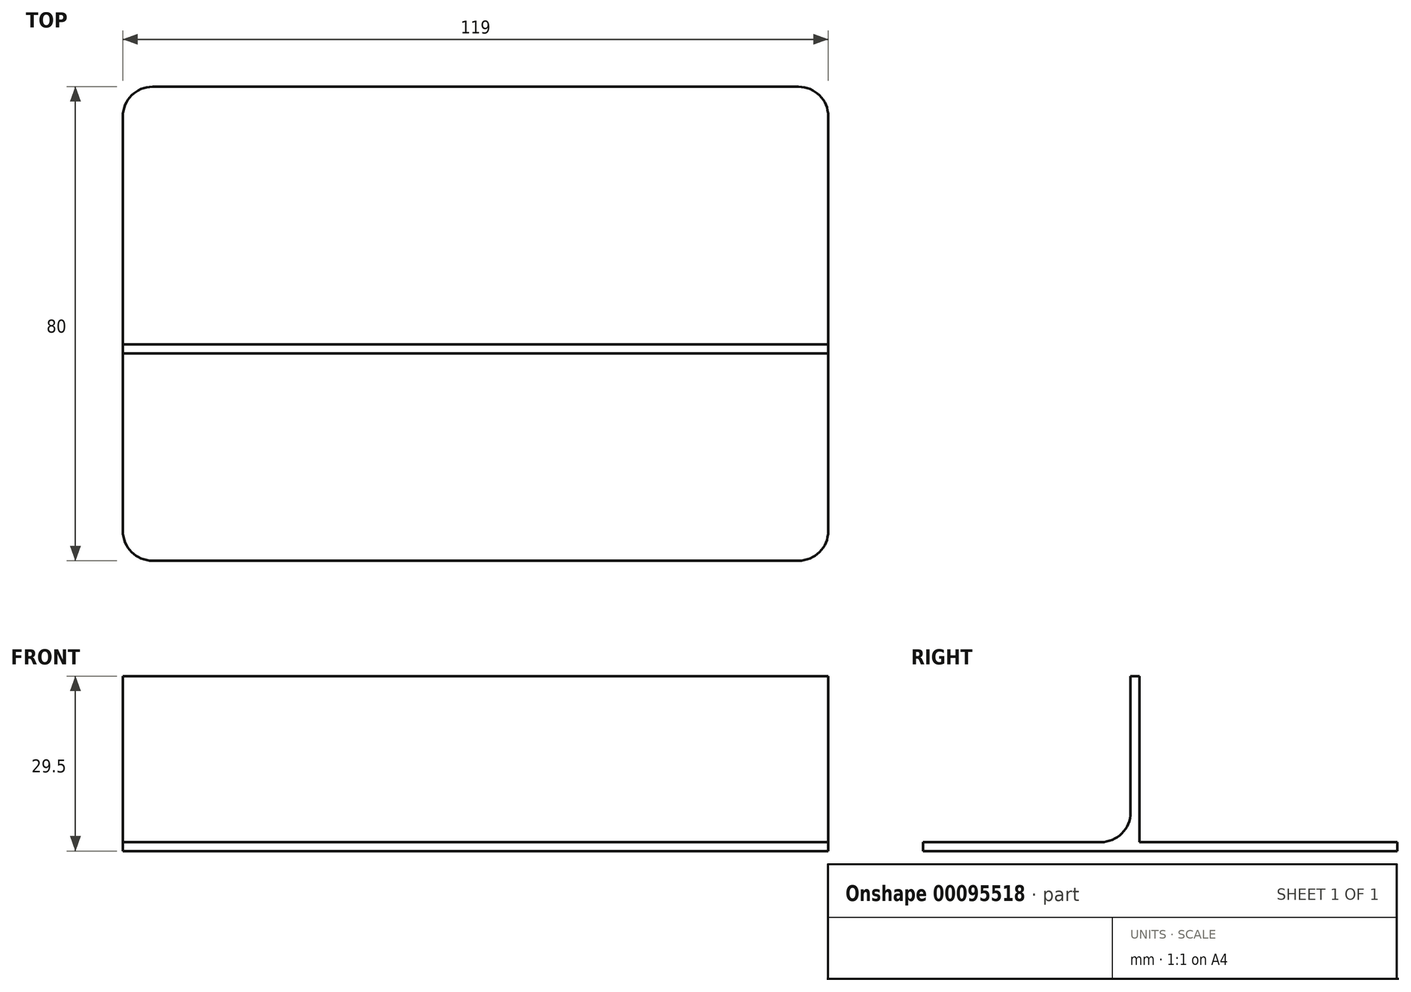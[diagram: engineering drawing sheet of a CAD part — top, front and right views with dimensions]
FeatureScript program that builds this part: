
annotation { "Feature Type Name" : "Feature", "Feature Type Description" : "" }
export const myFeature = defineFeature(function(context is Context, id is Id, definition is map)
    precondition{}
    {
        {
            var Q0;
            Q0=qCreatedBy(makeId("Top.planeOp"),FACE);
            var sketch = newSketch(context, id + "F0", { "sketchPlane" : qUnion([Q0])});
            skLineSegment(sketch, "E0.bottom", {"start": v(-85.63, 36.48) * mm, "end": v(33.37, 36.48) * mm});
            skLineSegment(sketch, "E0.top", {"start": v(-85.63, -43.52) * mm, "end": v(33.37, -43.52) * mm});
            skLineSegment(sketch, "E0.left", {"start": v(-85.63, 36.48) * mm, "end": v(-85.63, -43.52) * mm});
            skLineSegment(sketch, "E0.right", {"start": v(33.37, 36.48) * mm, "end": v(33.37, -43.52) * mm});
            skSolve(sketch);
        }
        {
            var Q0;
            Q0 = qSketchRegion(id + "F0", true);
            extrude(context, id + "F1", {"entities" : qUnion([Q0]), "depth" : 1.5 * mm});
        }
        {
            var Q0;
            Q0=makeQuery(id+"F1.opExtrude","SWEPT_EDGE",EDGE,{"disambiguationData":[OSD([sQuery(id+"F0.wireOp",EDGE,"E0.top"),sQuery(id+"F0.wireOp",EDGE,"E0.right")])]});
            var Q1;
            Q1=makeQuery(id+"F1.opExtrude","SWEPT_EDGE",EDGE,{"disambiguationData":[OSD([sQuery(id+"F0.wireOp",EDGE,"E0.bottom"),sQuery(id+"F0.wireOp",EDGE,"E0.right")])]});
            var Q2;
            Q2=makeQuery(id+"F1.opExtrude","SWEPT_EDGE",EDGE,{"disambiguationData":[OSD([sQuery(id+"F0.wireOp",EDGE,"E0.bottom"),sQuery(id+"F0.wireOp",EDGE,"E0.left")])]});
            var Q3;
            Q3=makeQuery(id+"F1.opExtrude","SWEPT_EDGE",EDGE,{"disambiguationData":[OSD([sQuery(id+"F0.wireOp",EDGE,"E0.top"),sQuery(id+"F0.wireOp",EDGE,"E0.left")])]});
            fillet(context, id + "F2", {"entities" : qUnion([Q0, Q1, Q2, Q3]), "radius" : 5 * mm, "tangentPropagation" : true, "allowEdgeOverflow" : false});
        }
        {
            var Q0;
            Q0=makeQuery(id+"F1.opExtrude","CAP_FACE",FACE,{"disambiguationData":[OSD([sQuery(id+"F0.wireOp",EDGE,"E0.bottom"),sQuery(id+"F0.wireOp",EDGE,"E0.top"),sQuery(id+"F0.wireOp",EDGE,"E0.left"),sQuery(id+"F0.wireOp",EDGE,"E0.right")])],"isStart":false});
            var sketch = newSketch(context, id + "F3", { "sketchPlane" : qUnion([Q0])});
            skLineSegment(sketch, "E1.bottom", {"start": v(33.37, -8.52) * mm, "end": v(-85.63, -8.52) * mm});
            skLineSegment(sketch, "E1.top", {"start": v(33.37, -7.02) * mm, "end": v(-85.63, -7.02) * mm});
            skLineSegment(sketch, "E1.left", {"start": v(33.37, -8.52) * mm, "end": v(33.37, -7.02) * mm});
            skLineSegment(sketch, "E1.right", {"start": v(-85.63, -8.52) * mm, "end": v(-85.63, -7.02) * mm});
            skSolve(sketch);
        }
        {
            var Q0;
            Q0 = qSketchRegion(id + "F3", true);
            extrude(context, id + "F4", {"entities" : qUnion([Q0]), "operationType" : NewBodyOperationType.ADD, "depth" : 28 * mm});
        }
        {
            var Q0;
            Q0=makeQuery(id+"F4.opExtrude","CAP_EDGE",EDGE,{"disambiguationData":[OSD([sQuery(id+"F3.wireOp",EDGE,"E1.top")])],"isStart":true});
            var Q1;
            Q1=makeQuery(id+"F4.opExtrude","CAP_EDGE",EDGE,{"disambiguationData":[OSD([sQuery(id+"F3.wireOp",EDGE,"E1.bottom")])],"isStart":true});
            fillet(context, id + "F5", {"entities" : qUnion([Q0, Q1]), "radius" : 5 * mm, "tangentPropagation" : true, "allowEdgeOverflow" : false});
        }
    });
